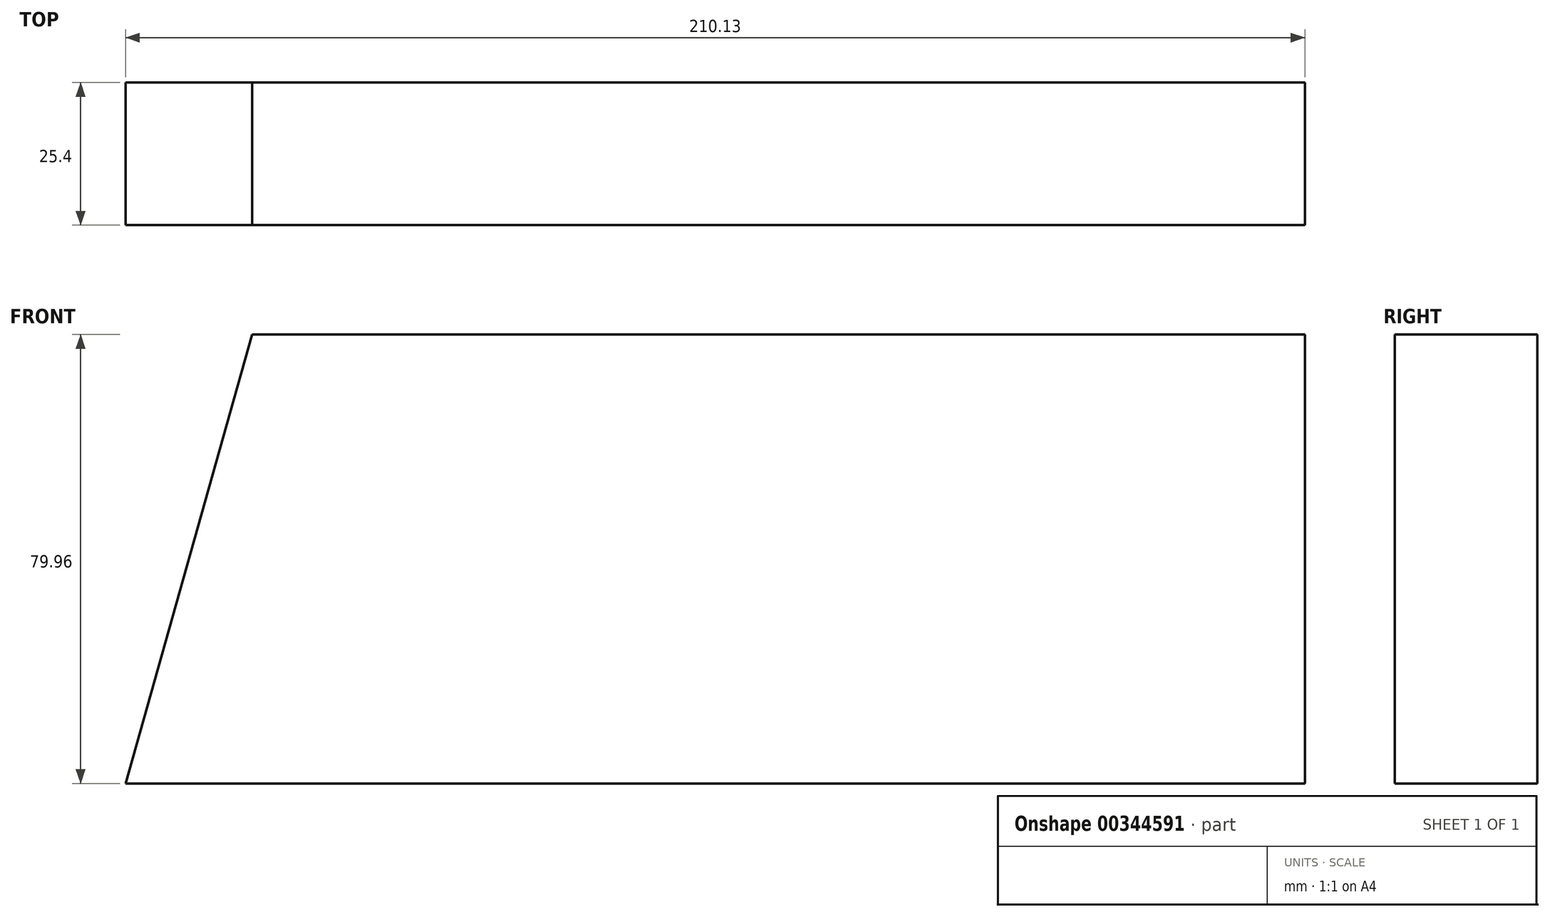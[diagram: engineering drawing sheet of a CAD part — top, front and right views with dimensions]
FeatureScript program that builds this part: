
annotation { "Feature Type Name" : "Feature", "Feature Type Description" : "" }
export const myFeature = defineFeature(function(context is Context, id is Id, definition is map)
    precondition{}
    {
        {
            var Q0;
            Q0=qCreatedBy(makeId("Front.planeOp"),FACE);
            var sketch = newSketch(context, id + "F0", { "sketchPlane" : qUnion([Q0])});
            skLineSegment(sketch, "E0", {"start": v(-109.24, 26.15) * mm, "end": v(78.3, 26.15) * mm});
            skLineSegment(sketch, "E1", {"start": v(78.3, 26.15) * mm, "end": v(78.3, -53.81) * mm});
            skLineSegment(sketch, "E2", {"start": v(78.3, -53.81) * mm, "end": v(-131.82, -53.81) * mm});
            skLineSegment(sketch, "E3", {"start": v(-131.82, -53.81) * mm, "end": v(-109.24, 26.15) * mm});
            skSolve(sketch);
        }
        {
            var Q0;
            Q0=makeQuery(id+"F0.imprint","IMPRINT",FACE,{"disambiguationData":[TD([[makeQuery(id+"F0.imprint","IMPRINT",EDGE,{"derivedFrom":sQuery(id+"F0.wireOp",EDGE,"E0")}),-1.0]])]});
            extrude(context, id + "F1", {"entities" : qUnion([Q0]), "depth" : 25.4 * mm});
        }
    });
